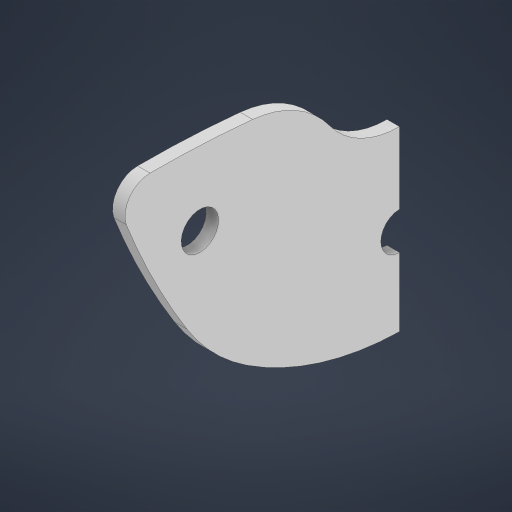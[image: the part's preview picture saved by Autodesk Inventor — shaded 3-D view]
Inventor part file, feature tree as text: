
AUTODESK INVENTOR PART (.ipt)
format: ipt  version: 2024 (Build 280153000, 153)  size: 216,064 bytes
history: native  units: in
note: dims shown in document units (in); Inventor stores cm internally (conversion verified against a paired STEP export)
features: sketch x1, extrude x1, hole x1
ambient origin geometry x8: Origin, YZ Plane, XZ Plane, XY Plane, X Axis, Y Axis, Z Axis, Center Point
bodies: Solid1 (feature_tree)
feature tree (3):
  sketch  "Sketch1"  dims[d0=0.5in d1=0.125in d2=1.0in d3=0.75in d4=1.0in d5=1.0in d6=0.5in d7=0.5in d8=1.25in d9=1.0in d10=1.0in d11=0.25in d12=0.25in d14=0.0in d15=0.0625in d16=0.75in d17=0.8108in d18=0.5635in d19=0.25in d20=0.375in d21=1.0in d22=0.1875in]
  extrude  "Extrusion1"  [1 undecoded]
  hole  "Hole1"  [1 undecoded]
note: 2 required parameter values undecoded (feature->parameter linkage not recoverable at this tier; creation-order binding heuristic only, values carry confidence <= 0.55)
